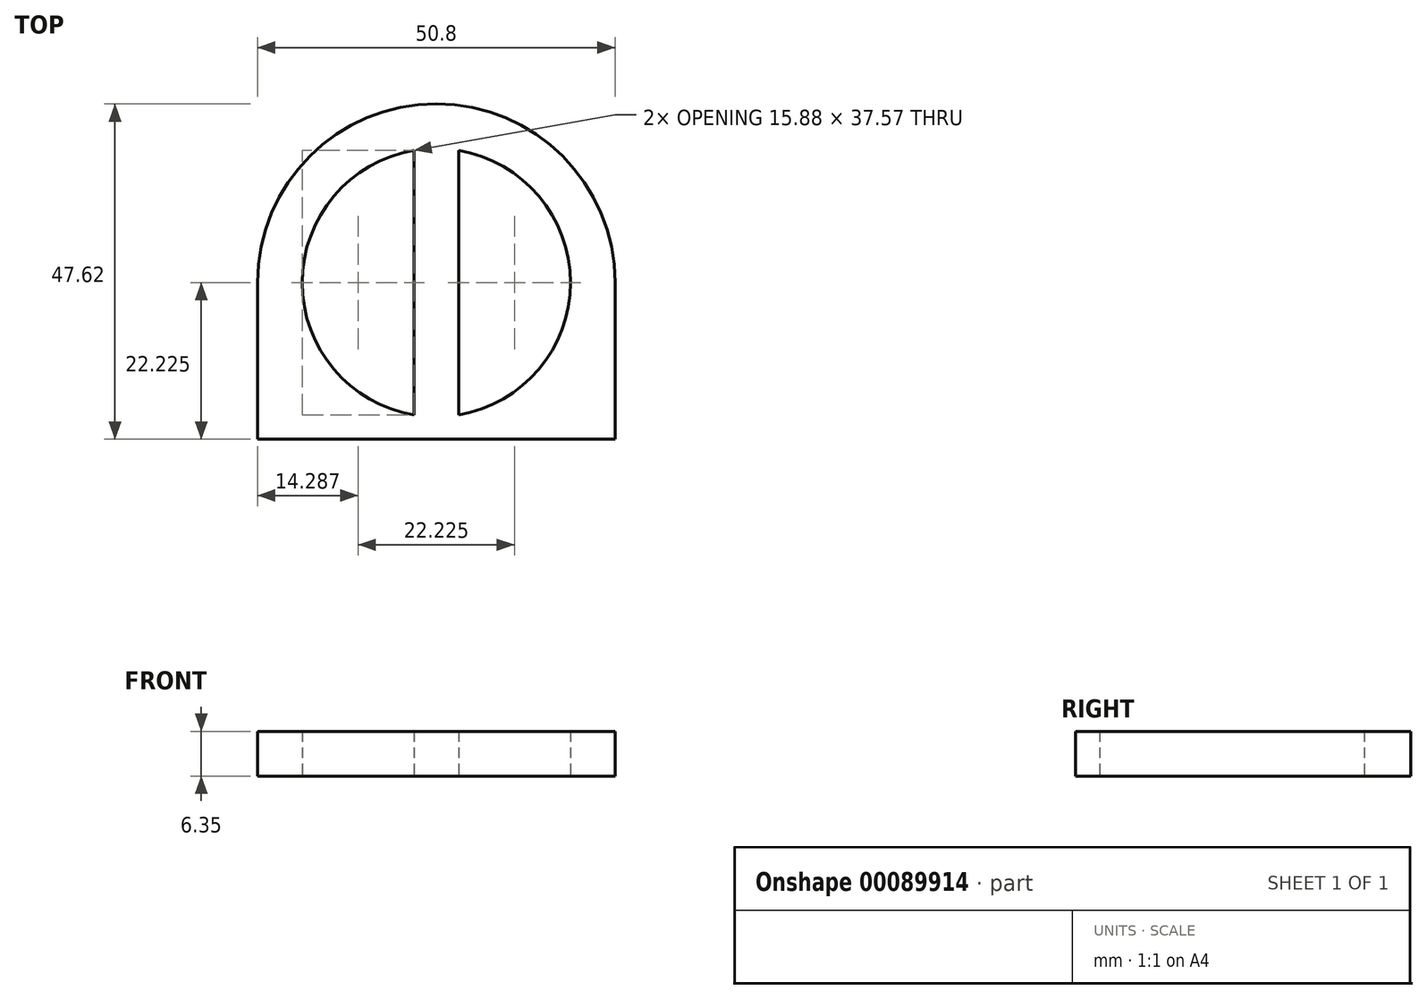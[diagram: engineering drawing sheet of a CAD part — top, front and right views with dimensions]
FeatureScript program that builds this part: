
annotation { "Feature Type Name" : "Feature", "Feature Type Description" : "" }
export const myFeature = defineFeature(function(context is Context, id is Id, definition is map)
    precondition{}
    {
        {
            var Q0;
            Q0=qCreatedBy(makeId("Top.planeOp"),FACE);
            var sketch = newSketch(context, id + "F0", { "sketchPlane" : qUnion([Q0])});
            skLineSegment(sketch, "E0", {"start": v(0, 0) * mm, "end": v(50.8, 0) * mm});
            skLineSegment(sketch, "E1", {"start": v(50.8, 0) * mm, "end": v(50.8, 22.23) * mm});
            skLineSegment(sketch, "E2", {"start": v(0, 0) * mm, "end": v(0, 22.23) * mm});
            skCircle(sketch, "E3", {"center": v(25.4, 22.23) * mm, "radius": 19.05 * mm});
            skArc(sketch, "E4", {"start": v(50.8, 22.23) * mm, "mid": v(25.4, 47.63) * mm, "end": v(0, 22.23) * mm});
            skSolve(sketch);
        }
        {
            var Q0;
            Q0 = qSketchRegion(id + "F0", true);
            extrude(context, id + "F1", {"entities" : qUnion([Q0]), "depth" : 6.35 * mm});
        }
        {
            var Q0;
            Q0=makeQuery(id+"F1.opExtrude","CAP_FACE",FACE,{"disambiguationData":[OSD([sQuery(id+"F0.wireOp",EDGE,"E0"),sQuery(id+"F0.wireOp",EDGE,"E1"),sQuery(id+"F0.wireOp",EDGE,"E2"),sQuery(id+"F0.wireOp",EDGE,"E3"),sQuery(id+"F0.wireOp",EDGE,"E4")])],"isStart":true});
            var sketch = newSketch(context, id + "F2", { "sketchPlane" : qUnion([Q0])});
            skLineSegment(sketch, "E5", {"start": v(28.58, 0) * mm, "end": v(22.23, 0) * mm});
            skLineSegment(sketch, "E6", {"start": v(22.23, 0) * mm, "end": v(22.23, -47.43) * mm});
            skLineSegment(sketch, "E7", {"start": v(28.58, 0) * mm, "end": v(28.58, -47.43) * mm});
            skArc(sketch, "E8", {"start": v(22.23, -47.43) * mm, "mid": v(25.4, -47.63) * mm, "end": v(28.58, -47.43) * mm});
            skSolve(sketch);
        }
        {
            var Q0;
            {var subQ0=sQuery(id+"F2.wireOp",EDGE,"E6");var subQ1=makeQuery(id+"F1.opExtrude","CAP_EDGE",EDGE,{"disambiguationData":[OSD([sQuery(id+"F0.wireOp",EDGE,"E3")])],"isStart":true});var subQ2=makeQuery(id+"F2.imprint","INTERSECT",VERTEX,{"disambiguationData":[OD(0.0)],"derivedFrom":[subQ1,subQ0]});Q0=makeQuery(id+"F2.imprint","IMPRINT",FACE,{"disambiguationData":[TD([[makeQuery(id+"F2.imprint","IMPRINT",EDGE,{"disambiguationData":[TD([[subQ2,-1.0]])],"derivedFrom":subQ0}),1.0]])]});}
            extrude(context, id + "F3", {"entities" : qUnion([Q0]), "operationType" : NewBodyOperationType.ADD, "oppositeDirection" : true, "depth" : 6.35 * mm});
        }
    });
